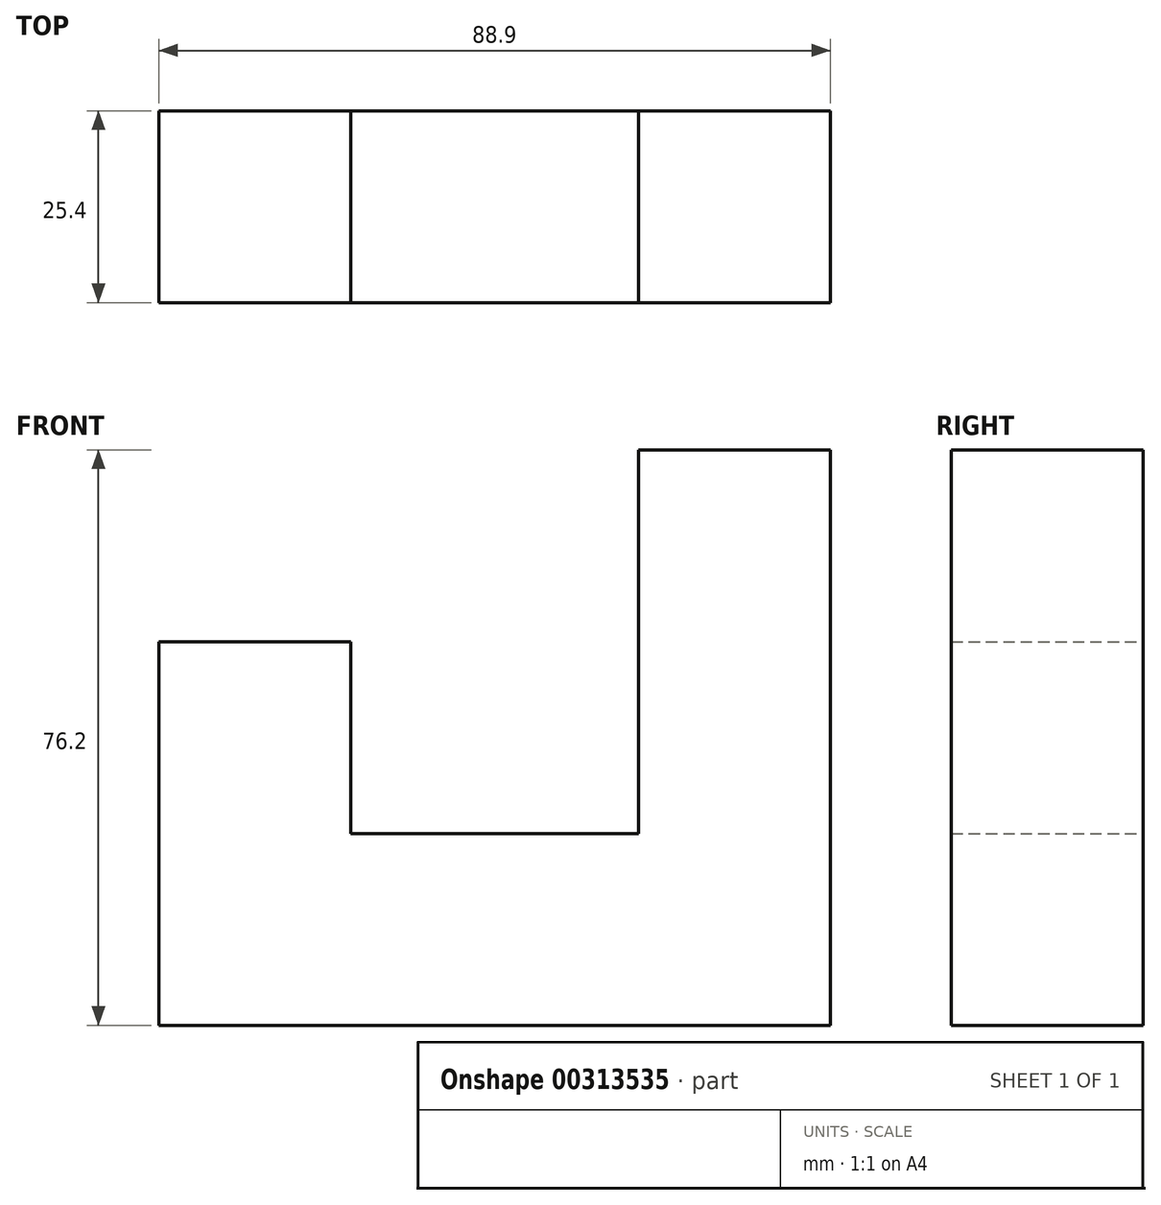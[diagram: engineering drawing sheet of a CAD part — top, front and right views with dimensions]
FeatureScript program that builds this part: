
annotation { "Feature Type Name" : "Feature", "Feature Type Description" : "" }
export const myFeature = defineFeature(function(context is Context, id is Id, definition is map)
    precondition{}
    {
        {
            var Q0;
            Q0=qCreatedBy(makeId("Front.planeOp"),FACE);
            var sketch = newSketch(context, id + "F0", { "sketchPlane" : qUnion([Q0])});
            skLineSegment(sketch, "E0", {"start": v(-60.56, -37.32) * mm, "end": v(28.34, -37.32) * mm});
            skLineSegment(sketch, "E1", {"start": v(28.34, -37.32) * mm, "end": v(28.34, 38.88) * mm});
            skLineSegment(sketch, "E2", {"start": v(-60.56, -37.32) * mm, "end": v(-60.56, 13.48) * mm});
            skLineSegment(sketch, "E3", {"start": v(-60.56, 13.48) * mm, "end": v(-35.16, 13.48) * mm});
            skLineSegment(sketch, "E4", {"start": v(2.94, 38.88) * mm, "end": v(28.34, 38.88) * mm});
            skLineSegment(sketch, "E5", {"start": v(-35.16, 13.48) * mm, "end": v(-35.16, -11.92) * mm});
            skLineSegment(sketch, "E6", {"start": v(2.94, 38.88) * mm, "end": v(2.94, -11.92) * mm});
            skLineSegment(sketch, "E7", {"start": v(-35.16, -11.92) * mm, "end": v(2.94, -11.92) * mm});
            skSolve(sketch);
        }
        {
            var Q0;
            Q0=makeQuery(id+"F0.imprint","IMPRINT",FACE,{"disambiguationData":[TD([[makeQuery(id+"F0.imprint","IMPRINT",EDGE,{"derivedFrom":sQuery(id+"F0.wireOp",EDGE,"E0")}),1.0]])]});
            extrude(context, id + "F1", {"entities" : qUnion([Q0]), "depth" : 25.4 * mm});
        }
    });
